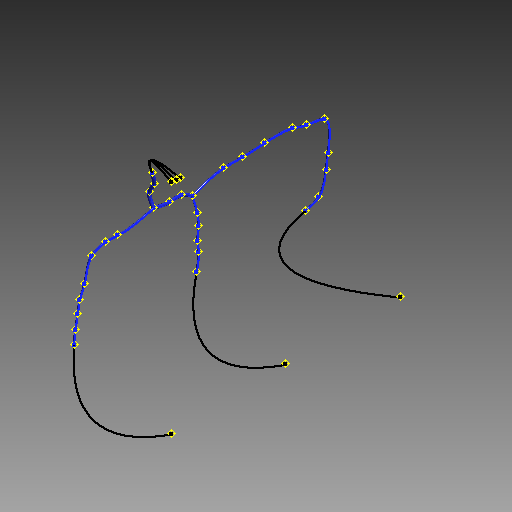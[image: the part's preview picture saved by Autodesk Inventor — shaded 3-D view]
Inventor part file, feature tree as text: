
AUTODESK INVENTOR PART (.ipt)
format: ipt  version: 2017 (Build 210142000, 142)  size: 375,808 bytes
history: native  units: mm (DEFAULTED — no unit token found)
features: other x49, plane x5, sketch x5, sweep x5
ambient origin geometry x8: Origin, YZ Plane, XZ Plane, XY Plane, X Axis, Y Axis, Z Axis, Center Point
bodies: Body1 (feature_tree), Body2 (feature_tree), Body3 (feature_tree), Body4 (feature_tree), Body5 (feature_tree)
feature tree (64):
  other  "Work Point1"
  other  "Work Point2"
  other  "Wire1"
  other  "Work Point3"
  other  "Work Point4"
  other  "Wire2"
  other  "Work Point5"
  other  "Work Point6"
  other  "Wire3"
  other  "Work Point7"
  other  "Work Point8"
  other  "Segment1"
  other  "Work Point9"
  other  "Work Point10"
  other  "Work Point11"
  other  "Work Point12"
  other  "Work Point13"
  other  "Work Point14"
  other  "Work Point15"
  other  "Work Point16"
  other  "Work Point17"
  other  "Work Point18"
  other  "Segment2"
  plane  "Work Plane3"
  other  "Work Point19"
  other  "Segment3"
  other  "Work Point20"
  other  "Work Point21"
  other  "Work Point22"
  other  "Work Point23"
  other  "Work Point24"
  other  "Work Point25"
  other  "Work Point26"
  other  "Work Point27"
  other  "Work Point28"
  plane  "Work Plane4"
  other  "Segment4"
  plane  "Work Plane5"
  plane  "Work Plane6"
  other  "Work Point29"
  other  "Segment5"
  other  "Work Point30"
  other  "Work Point31"
  other  "Work Point32"
  other  "Work Point33"
  other  "Work Point34"
  other  "Work Point35"
  other  "Work Point36"
  plane  "Work Plane7"
  sketch  "Sketch3"  dims[d4=0.0mm d5=0.0mm d6=0.0mm d7=0.0mm]
  other  "Srf3"
  sketch  "Sketch4"  dims[d8=0.0mm d9=0.0mm d10=0.0mm d11=0.0mm]
  other  "Srf4"
  sketch  "Sketch5"  dims[d12=0.0mm d13=0.0mm]
  other  "Srf5"
  sketch  "Sketch6"
  other  "Srf6"
  sketch  "Sketch7"
  other  "Srf7"
  sweep  "SweepSrf3"
  sweep  "SweepSrf4"
  sweep  "SweepSrf5"
  sweep  "SweepSrf6"
  sweep  "SweepSrf7"
